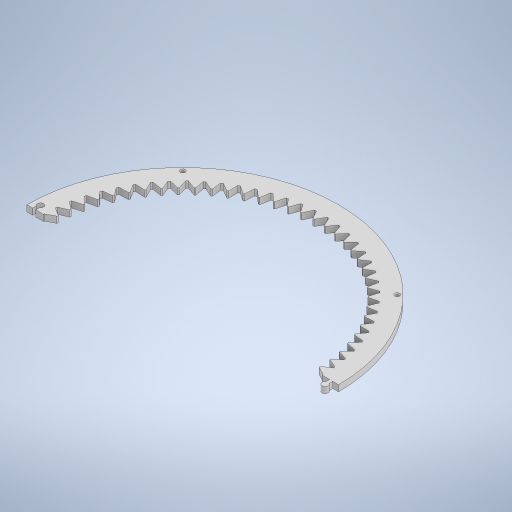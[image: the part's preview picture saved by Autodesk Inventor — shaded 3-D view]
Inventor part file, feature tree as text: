
AUTODESK INVENTOR PART (.ipt)
format: ipt  version: 2023 (Build 270158000, 158)  size: 516,608 bytes
history: native  units: in
note: dims shown in document units (in); Inventor stores cm internally (conversion verified against a paired STEP export)
features: sketch x2, extrude x1, hole x1
ambient origin geometry x8: Origin, YZ Plane, XZ Plane, XY Plane, X Axis, Y Axis, Z Axis, Center Point
bodies: Body1 (feature_tree)
feature tree (4):
  sketch  "Sketch1"  dims[d0=9.8425in d1=8.7992in]
  extrude  "Extrusion2"  Depth=8.7992in
  hole  "Hole1"  [1 undecoded]
  sketch  "Sketch2"  dims[d2=0.2953in d3=30.0deg d4=120.0deg d7=0.0394in d8=0.0394in d9=0.7874in d11=360.0deg d13=27.5591in d15=360.0deg d17=0.1969in d18=0.0in d19=9.311in d20=45.0deg d21=1.5748in d23=360.0deg d25=0.0945in d26=0.2362in d27=0.1575in d28=0.0787in d29=90.0deg d30=0.315in d31=0.8108in d32=9.8425in d33=8.7992in d34=9.2717in]
note: 1 required parameter value undecoded (feature->parameter linkage not recoverable at this tier; creation-order binding heuristic only, values carry confidence <= 0.55)
